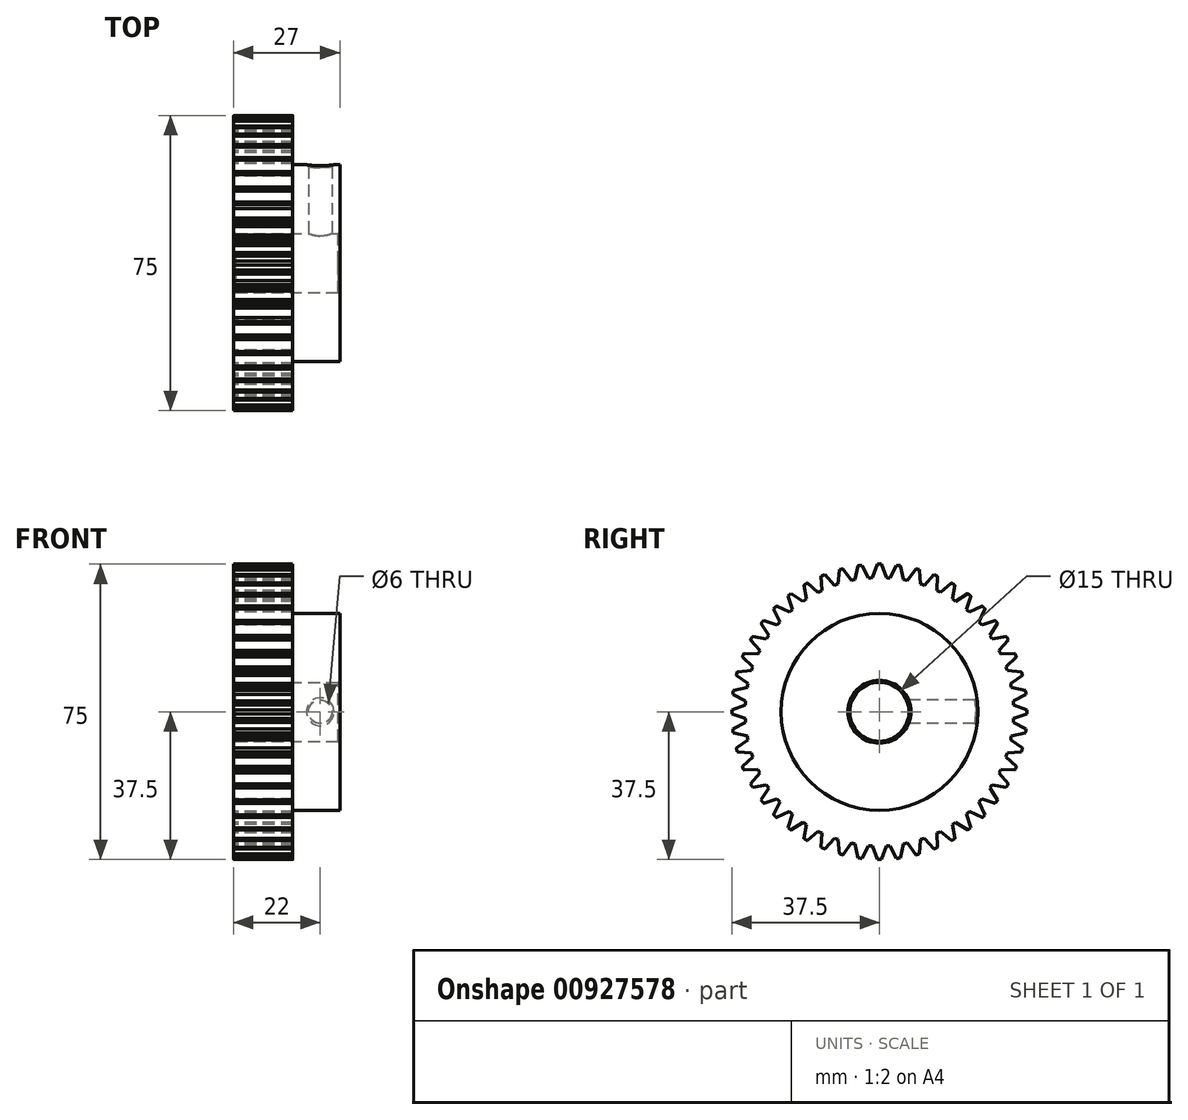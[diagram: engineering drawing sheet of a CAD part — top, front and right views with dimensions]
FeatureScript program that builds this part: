
annotation { "Feature Type Name" : "Feature", "Feature Type Description" : "" }
export const myFeature = defineFeature(function(context is Context, id is Id, definition is map)
    precondition{}
    {
        {
            var Q0;
            Q0=qCreatedBy(makeId("Right.planeOp"),FACE);
            var sketch = newSketch(context, id + "F0", { "sketchPlane" : qUnion([Q0])});
            skCircle(sketch, "E0", {"center": v(0, 0) * mm, "radius": 37.5 * mm});
            skSolve(sketch);
        }
        {
            var Q0;
            Q0 = qSketchRegion(id + "F0", true);
            extrude(context, id + "F1", {"entities" : qUnion([Q0]), "oppositeDirection" : true, "depth" : 27 * mm, "offsetDistance" : 25 * mm});
        }
        {
            var Q0;
            Q0=makeQuery(id+"F1.opExtrude","CAP_FACE",FACE,{"disambiguationData":[OSD([sQuery(id+"F0.wireOp",EDGE,"E0")])],"isStart":true});
            var sketch = newSketch(context, id + "F2", { "sketchPlane" : qUnion([Q0])});
            skCircle(sketch, "E1", {"center": v(0, 0) * mm, "radius": 7.5 * mm});
            skSolve(sketch);
        }
        {
            var Q0;
            Q0 = qSketchRegion(id + "F2", true);
            extrude(context, id + "F3", {"entities" : qUnion([Q0]), "operationType" : NewBodyOperationType.REMOVE, "endBound" : BoundingType.THROUGH_ALL, "oppositeDirection" : true, "depth" : 25 * mm, "offsetDistance" : 25 * mm});
        }
        {
            var Q0;
            Q0=makeQuery(id+"F3.boolean.opBoolean","COPY",FACE,{"derivedFrom":makeQuery(id+"F3.opExtrude","SWEPT_FACE",FACE,{"disambiguationData":[OSD([sQuery(id+"F2.wireOp",EDGE,"E1")])]})});
            chamfer(context, id + "F4", {"entities" : qUnion([Q0]), "width" : 0.5 * mm, "tangentPropagation" : true});
        }
        {
            var Q0;
            Q0=makeQuery(id+"F1.opExtrude","CAP_FACE",FACE,{"disambiguationData":[OSD([sQuery(id+"F0.wireOp",EDGE,"E0")])],"isStart":true});
            var sketch = newSketch(context, id + "F5", { "sketchPlane" : qUnion([Q0])});
            skCircle(sketch, "E2", {"center": v(0, 0) * mm, "radius": 25 * mm});
            skSolve(sketch);
        }
        {
            var Q0;
            Q0=makeQuery(id+"F5.imprint","IMPRINT",FACE,{"disambiguationData":[TD([[makeQuery(id+"F5.imprint","IMPRINT",EDGE,{"derivedFrom":sQuery(id+"F5.wireOp",EDGE,"E2")}),-1.0]])]});
            extrude(context, id + "F6", {"entities" : qUnion([Q0]), "operationType" : NewBodyOperationType.REMOVE, "oppositeDirection" : true, "depth" : 12 * mm, "offsetDistance" : 25 * mm});
        }
        {
            var Q0;
            Q0=makeQuery(id+"F1.opExtrude","CAP_FACE",FACE,{"disambiguationData":[OSD([sQuery(id+"F0.wireOp",EDGE,"E0")])],"isStart":false});
            var sketch = newSketch(context, id + "F7", { "sketchPlane" : qUnion([Q0])});
            skCircle(sketch, "E3", {"center": v(0, 0) * mm, "radius": 34.12 * mm, "construction": true});
            skLineSegment(sketch, "E4", {"start": v(0, 50.65) * mm, "end": v(0, 0) * mm, "construction": true});
            skLineSegment(sketch, "E5", {"start": v(0, 0) * mm, "end": v(6.76, 51.35) * mm, "construction": true});
            skLineSegment(sketch, "E6", {"start": v(0, 0) * mm, "end": v(3.18, 48.48) * mm, "construction": true});
            skLineSegment(sketch, "E7", {"start": v(0, 37.5) * mm, "end": v(0.5, 37.5) * mm});
            skLineSegment(sketch, "E8", {"start": v(4.9, 37.18) * mm, "end": v(4.4, 37.24) * mm});
            skLineSegment(sketch, "E9", {"start": v(2.23, 34.05) * mm, "end": v(2.73, 34.02) * mm});
            skLineSegment(sketch, "E10.MirrorCS", {"start": v(2.23, 34.05) * mm, "end": v(1.73, 34.08) * mm});
            skLineSegment(sketch, "E11", {"start": v(4.4, 37.24) * mm, "end": v(2.73, 34.02) * mm});
            skLineSegment(sketch, "E12", {"start": v(0.5, 37.5) * mm, "end": v(1.73, 34.08) * mm});
            skLineSegment(sketch, "E13.1.0", {"start": v(0, 0) * mm, "end": v(0, 51.8) * mm, "construction": true});
            skLineSegment(sketch, "E13.1.1", {"start": v(0, 37.5) * mm, "end": v(-0.5, 37.5) * mm});
            skLineSegment(sketch, "E13.1.2", {"start": v(-0.5, 37.5) * mm, "end": v(-1.73, 34.08) * mm});
            skLineSegment(sketch, "E13.1.3", {"start": v(-2.23, 34.05) * mm, "end": v(-1.73, 34.08) * mm});
            skLineSegment(sketch, "E13.1.4", {"start": v(-2.23, 34.05) * mm, "end": v(-2.73, 34.02) * mm});
            skLineSegment(sketch, "E13.1.5", {"start": v(-4.4, 37.24) * mm, "end": v(-2.73, 34.02) * mm});
            skLineSegment(sketch, "E13.1.6", {"start": v(-4.9, 37.18) * mm, "end": v(-4.4, 37.24) * mm});
            skLineSegment(sketch, "E13.2.0", {"start": v(0, 0) * mm, "end": v(-6.76, 51.35) * mm, "construction": true});
            skLineSegment(sketch, "E13.2.1", {"start": v(-4.9, 37.18) * mm, "end": v(-5.4, 37.11) * mm});
            skLineSegment(sketch, "E13.2.2", {"start": v(-5.4, 37.11) * mm, "end": v(-6.17, 33.56) * mm});
            skLineSegment(sketch, "E13.2.3", {"start": v(-6.66, 33.47) * mm, "end": v(-6.17, 33.56) * mm});
            skLineSegment(sketch, "E13.2.4", {"start": v(-6.66, 33.47) * mm, "end": v(-7.15, 33.37) * mm});
            skLineSegment(sketch, "E13.2.5", {"start": v(-9.22, 36.35) * mm, "end": v(-7.15, 33.37) * mm});
            skLineSegment(sketch, "E13.2.6", {"start": v(-9.7, 36.22) * mm, "end": v(-9.22, 36.35) * mm});
            skLineSegment(sketch, "E13.3.0", {"start": v(0, 0) * mm, "end": v(-13.4, 50.03) * mm, "construction": true});
            skLineSegment(sketch, "E13.3.1", {"start": v(-9.7, 36.22) * mm, "end": v(-10.19, 36.09) * mm});
            skLineSegment(sketch, "E13.3.2", {"start": v(-10.19, 36.09) * mm, "end": v(-10.5, 32.47) * mm});
            skLineSegment(sketch, "E13.3.3", {"start": v(-10.97, 32.31) * mm, "end": v(-10.5, 32.47) * mm});
            skLineSegment(sketch, "E13.3.4", {"start": v(-10.97, 32.31) * mm, "end": v(-11.44, 32.15) * mm});
            skLineSegment(sketch, "E13.3.5", {"start": v(-13.89, 34.83) * mm, "end": v(-11.44, 32.15) * mm});
            skLineSegment(sketch, "E13.3.6", {"start": v(-14.35, 34.65) * mm, "end": v(-13.89, 34.83) * mm});
            skLineSegment(sketch, "E13.4.0", {"start": v(0, 0) * mm, "end": v(-19.82, 47.85) * mm, "construction": true});
            skLineSegment(sketch, "E13.4.1", {"start": v(-14.35, 34.65) * mm, "end": v(-14.81, 34.45) * mm});
            skLineSegment(sketch, "E13.4.2", {"start": v(-14.81, 34.45) * mm, "end": v(-14.64, 30.82) * mm});
            skLineSegment(sketch, "E13.4.3", {"start": v(-15.1, 30.6) * mm, "end": v(-14.64, 30.82) * mm});
            skLineSegment(sketch, "E13.4.4", {"start": v(-15.1, 30.6) * mm, "end": v(-15.54, 30.38) * mm});
            skLineSegment(sketch, "E13.4.5", {"start": v(-18.32, 32.72) * mm, "end": v(-15.54, 30.38) * mm});
            skLineSegment(sketch, "E13.4.6", {"start": v(-18.75, 32.48) * mm, "end": v(-18.32, 32.72) * mm});
            skLineSegment(sketch, "E13.5.0", {"start": v(0, 0) * mm, "end": v(-25.9, 44.85) * mm, "construction": true});
            skLineSegment(sketch, "E13.5.1", {"start": v(-18.75, 32.48) * mm, "end": v(-19.18, 32.22) * mm});
            skLineSegment(sketch, "E13.5.2", {"start": v(-19.18, 32.22) * mm, "end": v(-18.54, 28.65) * mm});
            skLineSegment(sketch, "E13.5.3", {"start": v(-18.96, 28.37) * mm, "end": v(-18.54, 28.65) * mm});
            skLineSegment(sketch, "E13.5.4", {"start": v(-18.96, 28.37) * mm, "end": v(-19.37, 28.1) * mm});
            skLineSegment(sketch, "E13.5.5", {"start": v(-22.43, 30.05) * mm, "end": v(-19.37, 28.1) * mm});
            skLineSegment(sketch, "E13.5.6", {"start": v(-22.83, 29.75) * mm, "end": v(-22.43, 30.05) * mm});
            skLineSegment(sketch, "E13.6.0", {"start": v(0, 0) * mm, "end": v(-31.53, 41.09) * mm, "construction": true});
            skLineSegment(sketch, "E13.6.1", {"start": v(-22.83, 29.75) * mm, "end": v(-23.22, 29.44) * mm});
            skLineSegment(sketch, "E13.6.2", {"start": v(-23.22, 29.44) * mm, "end": v(-22.12, 25.98) * mm});
            skLineSegment(sketch, "E13.6.3", {"start": v(-22.5, 25.66) * mm, "end": v(-22.12, 25.98) * mm});
            skLineSegment(sketch, "E13.6.4", {"start": v(-22.5, 25.66) * mm, "end": v(-22.87, 25.32) * mm});
            skLineSegment(sketch, "E13.6.5", {"start": v(-26.16, 26.87) * mm, "end": v(-22.87, 25.32) * mm});
            skLineSegment(sketch, "E13.6.6", {"start": v(-26.52, 26.52) * mm, "end": v(-26.16, 26.87) * mm});
            skLineSegment(sketch, "E13.7.0", {"start": v(0, 0) * mm, "end": v(-36.62, 36.62) * mm, "construction": true});
            skLineSegment(sketch, "E13.7.1", {"start": v(-26.52, 26.52) * mm, "end": v(-26.87, 26.16) * mm});
            skLineSegment(sketch, "E13.7.2", {"start": v(-26.87, 26.16) * mm, "end": v(-25.32, 22.87) * mm});
            skLineSegment(sketch, "E13.7.3", {"start": v(-25.66, 22.5) * mm, "end": v(-25.32, 22.87) * mm});
            skLineSegment(sketch, "E13.7.4", {"start": v(-25.66, 22.5) * mm, "end": v(-25.98, 22.12) * mm});
            skLineSegment(sketch, "E13.7.5", {"start": v(-29.44, 23.22) * mm, "end": v(-25.98, 22.12) * mm});
            skLineSegment(sketch, "E13.7.6", {"start": v(-29.75, 22.83) * mm, "end": v(-29.44, 23.22) * mm});
            skLineSegment(sketch, "E13.8.0", {"start": v(0, 0) * mm, "end": v(-41.09, 31.53) * mm, "construction": true});
            skLineSegment(sketch, "E13.8.1", {"start": v(-29.75, 22.83) * mm, "end": v(-30.05, 22.43) * mm});
            skLineSegment(sketch, "E13.8.2", {"start": v(-30.05, 22.43) * mm, "end": v(-28.1, 19.37) * mm});
            skLineSegment(sketch, "E13.8.3", {"start": v(-28.37, 18.96) * mm, "end": v(-28.1, 19.37) * mm});
            skLineSegment(sketch, "E13.8.4", {"start": v(-28.37, 18.96) * mm, "end": v(-28.65, 18.54) * mm});
            skLineSegment(sketch, "E13.8.5", {"start": v(-32.22, 19.18) * mm, "end": v(-28.65, 18.54) * mm});
            skLineSegment(sketch, "E13.8.6", {"start": v(-32.48, 18.75) * mm, "end": v(-32.22, 19.18) * mm});
            skLineSegment(sketch, "E13.9.0", {"start": v(0, 0) * mm, "end": v(-44.85, 25.9) * mm, "construction": true});
            skLineSegment(sketch, "E13.9.1", {"start": v(-32.48, 18.75) * mm, "end": v(-32.72, 18.32) * mm});
            skLineSegment(sketch, "E13.9.2", {"start": v(-32.72, 18.32) * mm, "end": v(-30.38, 15.54) * mm});
            skLineSegment(sketch, "E13.9.3", {"start": v(-30.6, 15.1) * mm, "end": v(-30.38, 15.54) * mm});
            skLineSegment(sketch, "E13.9.4", {"start": v(-30.6, 15.1) * mm, "end": v(-30.82, 14.64) * mm});
            skLineSegment(sketch, "E13.9.5", {"start": v(-34.45, 14.81) * mm, "end": v(-30.82, 14.64) * mm});
            skLineSegment(sketch, "E13.9.6", {"start": v(-34.65, 14.35) * mm, "end": v(-34.45, 14.81) * mm});
            skLineSegment(sketch, "E13.10.0", {"start": v(0, 0) * mm, "end": v(-47.85, 19.82) * mm, "construction": true});
            skLineSegment(sketch, "E13.10.1", {"start": v(-34.65, 14.35) * mm, "end": v(-34.83, 13.89) * mm});
            skLineSegment(sketch, "E13.10.2", {"start": v(-34.83, 13.89) * mm, "end": v(-32.15, 11.44) * mm});
            skLineSegment(sketch, "E13.10.3", {"start": v(-32.31, 10.97) * mm, "end": v(-32.15, 11.44) * mm});
            skLineSegment(sketch, "E13.10.4", {"start": v(-32.31, 10.97) * mm, "end": v(-32.47, 10.5) * mm});
            skLineSegment(sketch, "E13.10.5", {"start": v(-36.09, 10.19) * mm, "end": v(-32.47, 10.5) * mm});
            skLineSegment(sketch, "E13.10.6", {"start": v(-36.22, 9.7) * mm, "end": v(-36.09, 10.19) * mm});
            skLineSegment(sketch, "E13.11.0", {"start": v(0, 0) * mm, "end": v(-50.03, 13.4) * mm, "construction": true});
            skLineSegment(sketch, "E13.11.1", {"start": v(-36.22, 9.7) * mm, "end": v(-36.35, 9.22) * mm});
            skLineSegment(sketch, "E13.11.2", {"start": v(-36.35, 9.22) * mm, "end": v(-33.37, 7.15) * mm});
            skLineSegment(sketch, "E13.11.3", {"start": v(-33.47, 6.66) * mm, "end": v(-33.37, 7.15) * mm});
            skLineSegment(sketch, "E13.11.4", {"start": v(-33.47, 6.66) * mm, "end": v(-33.56, 6.17) * mm});
            skLineSegment(sketch, "E13.11.5", {"start": v(-37.11, 5.4) * mm, "end": v(-33.56, 6.17) * mm});
            skLineSegment(sketch, "E13.11.6", {"start": v(-37.18, 4.9) * mm, "end": v(-37.11, 5.4) * mm});
            skLineSegment(sketch, "E13.12.0", {"start": v(0, 0) * mm, "end": v(-51.35, 6.76) * mm, "construction": true});
            skLineSegment(sketch, "E13.12.1", {"start": v(-37.18, 4.9) * mm, "end": v(-37.24, 4.4) * mm});
            skLineSegment(sketch, "E13.12.2", {"start": v(-37.24, 4.4) * mm, "end": v(-34.02, 2.73) * mm});
            skLineSegment(sketch, "E13.12.3", {"start": v(-34.05, 2.23) * mm, "end": v(-34.02, 2.73) * mm});
            skLineSegment(sketch, "E13.12.4", {"start": v(-34.05, 2.23) * mm, "end": v(-34.08, 1.73) * mm});
            skLineSegment(sketch, "E13.12.5", {"start": v(-37.5, 0.5) * mm, "end": v(-34.08, 1.73) * mm});
            skLineSegment(sketch, "E13.12.6", {"start": v(-37.5, 0) * mm, "end": v(-37.5, 0.5) * mm});
            skLineSegment(sketch, "E13.13.0", {"start": v(0, 0) * mm, "end": v(-51.8, 0) * mm, "construction": true});
            skLineSegment(sketch, "E13.13.1", {"start": v(-37.5, 0) * mm, "end": v(-37.5, -0.5) * mm});
            skLineSegment(sketch, "E13.13.2", {"start": v(-37.5, -0.5) * mm, "end": v(-34.08, -1.73) * mm});
            skLineSegment(sketch, "E13.13.3", {"start": v(-34.05, -2.23) * mm, "end": v(-34.08, -1.73) * mm});
            skLineSegment(sketch, "E13.13.4", {"start": v(-34.05, -2.23) * mm, "end": v(-34.02, -2.73) * mm});
            skLineSegment(sketch, "E13.13.5", {"start": v(-37.24, -4.4) * mm, "end": v(-34.02, -2.73) * mm});
            skLineSegment(sketch, "E13.13.6", {"start": v(-37.18, -4.9) * mm, "end": v(-37.24, -4.4) * mm});
            skLineSegment(sketch, "E13.14.0", {"start": v(0, 0) * mm, "end": v(-51.35, -6.76) * mm, "construction": true});
            skLineSegment(sketch, "E13.14.1", {"start": v(-37.18, -4.9) * mm, "end": v(-37.11, -5.4) * mm});
            skLineSegment(sketch, "E13.14.2", {"start": v(-37.11, -5.4) * mm, "end": v(-33.56, -6.17) * mm});
            skLineSegment(sketch, "E13.14.3", {"start": v(-33.47, -6.66) * mm, "end": v(-33.56, -6.17) * mm});
            skLineSegment(sketch, "E13.14.4", {"start": v(-33.47, -6.66) * mm, "end": v(-33.37, -7.15) * mm});
            skLineSegment(sketch, "E13.14.5", {"start": v(-36.35, -9.22) * mm, "end": v(-33.37, -7.15) * mm});
            skLineSegment(sketch, "E13.14.6", {"start": v(-36.22, -9.7) * mm, "end": v(-36.35, -9.22) * mm});
            skLineSegment(sketch, "E13.15.0", {"start": v(0, 0) * mm, "end": v(-50.03, -13.4) * mm, "construction": true});
            skLineSegment(sketch, "E13.15.1", {"start": v(-36.22, -9.7) * mm, "end": v(-36.09, -10.19) * mm});
            skLineSegment(sketch, "E13.15.2", {"start": v(-36.09, -10.19) * mm, "end": v(-32.47, -10.5) * mm});
            skLineSegment(sketch, "E13.15.3", {"start": v(-32.31, -10.97) * mm, "end": v(-32.47, -10.5) * mm});
            skLineSegment(sketch, "E13.15.4", {"start": v(-32.31, -10.97) * mm, "end": v(-32.15, -11.44) * mm});
            skLineSegment(sketch, "E13.15.5", {"start": v(-34.83, -13.89) * mm, "end": v(-32.15, -11.44) * mm});
            skLineSegment(sketch, "E13.15.6", {"start": v(-34.65, -14.35) * mm, "end": v(-34.83, -13.89) * mm});
            skLineSegment(sketch, "E13.16.0", {"start": v(0, 0) * mm, "end": v(-47.85, -19.82) * mm, "construction": true});
            skLineSegment(sketch, "E13.16.1", {"start": v(-34.65, -14.35) * mm, "end": v(-34.45, -14.81) * mm});
            skLineSegment(sketch, "E13.16.2", {"start": v(-34.45, -14.81) * mm, "end": v(-30.82, -14.64) * mm});
            skLineSegment(sketch, "E13.16.3", {"start": v(-30.6, -15.1) * mm, "end": v(-30.82, -14.64) * mm});
            skLineSegment(sketch, "E13.16.4", {"start": v(-30.6, -15.1) * mm, "end": v(-30.38, -15.54) * mm});
            skLineSegment(sketch, "E13.16.5", {"start": v(-32.72, -18.32) * mm, "end": v(-30.38, -15.54) * mm});
            skLineSegment(sketch, "E13.16.6", {"start": v(-32.48, -18.75) * mm, "end": v(-32.72, -18.32) * mm});
            skLineSegment(sketch, "E13.17.0", {"start": v(0, 0) * mm, "end": v(-44.85, -25.9) * mm, "construction": true});
            skLineSegment(sketch, "E13.17.1", {"start": v(-32.48, -18.75) * mm, "end": v(-32.22, -19.18) * mm});
            skLineSegment(sketch, "E13.17.2", {"start": v(-32.22, -19.18) * mm, "end": v(-28.65, -18.54) * mm});
            skLineSegment(sketch, "E13.17.3", {"start": v(-28.37, -18.96) * mm, "end": v(-28.65, -18.54) * mm});
            skLineSegment(sketch, "E13.17.4", {"start": v(-28.37, -18.96) * mm, "end": v(-28.1, -19.37) * mm});
            skLineSegment(sketch, "E13.17.5", {"start": v(-30.05, -22.43) * mm, "end": v(-28.1, -19.37) * mm});
            skLineSegment(sketch, "E13.17.6", {"start": v(-29.75, -22.83) * mm, "end": v(-30.05, -22.43) * mm});
            skLineSegment(sketch, "E13.18.0", {"start": v(0, 0) * mm, "end": v(-41.09, -31.53) * mm, "construction": true});
            skLineSegment(sketch, "E13.18.1", {"start": v(-29.75, -22.83) * mm, "end": v(-29.44, -23.22) * mm});
            skLineSegment(sketch, "E13.18.2", {"start": v(-29.44, -23.22) * mm, "end": v(-25.98, -22.12) * mm});
            skLineSegment(sketch, "E13.18.3", {"start": v(-25.66, -22.5) * mm, "end": v(-25.98, -22.12) * mm});
            skLineSegment(sketch, "E13.18.4", {"start": v(-25.66, -22.5) * mm, "end": v(-25.32, -22.87) * mm});
            skLineSegment(sketch, "E13.18.5", {"start": v(-26.87, -26.16) * mm, "end": v(-25.32, -22.87) * mm});
            skLineSegment(sketch, "E13.18.6", {"start": v(-26.52, -26.52) * mm, "end": v(-26.87, -26.16) * mm});
            skLineSegment(sketch, "E13.19.0", {"start": v(0, 0) * mm, "end": v(-36.62, -36.62) * mm, "construction": true});
            skLineSegment(sketch, "E13.19.1", {"start": v(-26.52, -26.52) * mm, "end": v(-26.16, -26.87) * mm});
            skLineSegment(sketch, "E13.19.2", {"start": v(-26.16, -26.87) * mm, "end": v(-22.87, -25.32) * mm});
            skLineSegment(sketch, "E13.19.3", {"start": v(-22.5, -25.66) * mm, "end": v(-22.87, -25.32) * mm});
            skLineSegment(sketch, "E13.19.4", {"start": v(-22.5, -25.66) * mm, "end": v(-22.12, -25.98) * mm});
            skLineSegment(sketch, "E13.19.5", {"start": v(-23.22, -29.44) * mm, "end": v(-22.12, -25.98) * mm});
            skLineSegment(sketch, "E13.19.6", {"start": v(-22.83, -29.75) * mm, "end": v(-23.22, -29.44) * mm});
            skLineSegment(sketch, "E13.20.0", {"start": v(0, 0) * mm, "end": v(-31.53, -41.09) * mm, "construction": true});
            skLineSegment(sketch, "E13.20.1", {"start": v(-22.83, -29.75) * mm, "end": v(-22.43, -30.05) * mm});
            skLineSegment(sketch, "E13.20.2", {"start": v(-22.43, -30.05) * mm, "end": v(-19.37, -28.1) * mm});
            skLineSegment(sketch, "E13.20.3", {"start": v(-18.96, -28.37) * mm, "end": v(-19.37, -28.1) * mm});
            skLineSegment(sketch, "E13.20.4", {"start": v(-18.96, -28.37) * mm, "end": v(-18.54, -28.65) * mm});
            skLineSegment(sketch, "E13.20.5", {"start": v(-19.18, -32.22) * mm, "end": v(-18.54, -28.65) * mm});
            skLineSegment(sketch, "E13.20.6", {"start": v(-18.75, -32.48) * mm, "end": v(-19.18, -32.22) * mm});
            skLineSegment(sketch, "E13.21.0", {"start": v(0, 0) * mm, "end": v(-25.9, -44.85) * mm, "construction": true});
            skLineSegment(sketch, "E13.21.1", {"start": v(-18.75, -32.48) * mm, "end": v(-18.32, -32.72) * mm});
            skLineSegment(sketch, "E13.21.2", {"start": v(-18.32, -32.72) * mm, "end": v(-15.54, -30.38) * mm});
            skLineSegment(sketch, "E13.21.3", {"start": v(-15.1, -30.6) * mm, "end": v(-15.54, -30.38) * mm});
            skLineSegment(sketch, "E13.21.4", {"start": v(-15.1, -30.6) * mm, "end": v(-14.64, -30.82) * mm});
            skLineSegment(sketch, "E13.21.5", {"start": v(-14.81, -34.45) * mm, "end": v(-14.64, -30.82) * mm});
            skLineSegment(sketch, "E13.21.6", {"start": v(-14.35, -34.65) * mm, "end": v(-14.81, -34.45) * mm});
            skLineSegment(sketch, "E13.22.0", {"start": v(0, 0) * mm, "end": v(-19.82, -47.85) * mm, "construction": true});
            skLineSegment(sketch, "E13.22.1", {"start": v(-14.35, -34.65) * mm, "end": v(-13.89, -34.83) * mm});
            skLineSegment(sketch, "E13.22.2", {"start": v(-13.89, -34.83) * mm, "end": v(-11.44, -32.15) * mm});
            skLineSegment(sketch, "E13.22.3", {"start": v(-10.97, -32.31) * mm, "end": v(-11.44, -32.15) * mm});
            skLineSegment(sketch, "E13.22.4", {"start": v(-10.97, -32.31) * mm, "end": v(-10.5, -32.47) * mm});
            skLineSegment(sketch, "E13.22.5", {"start": v(-10.19, -36.09) * mm, "end": v(-10.5, -32.47) * mm});
            skLineSegment(sketch, "E13.22.6", {"start": v(-9.7, -36.22) * mm, "end": v(-10.19, -36.09) * mm});
            skLineSegment(sketch, "E13.23.0", {"start": v(0, 0) * mm, "end": v(-13.4, -50.03) * mm, "construction": true});
            skLineSegment(sketch, "E13.23.1", {"start": v(-9.7, -36.22) * mm, "end": v(-9.22, -36.35) * mm});
            skLineSegment(sketch, "E13.23.2", {"start": v(-9.22, -36.35) * mm, "end": v(-7.15, -33.37) * mm});
            skLineSegment(sketch, "E13.23.3", {"start": v(-6.66, -33.47) * mm, "end": v(-7.15, -33.37) * mm});
            skLineSegment(sketch, "E13.23.4", {"start": v(-6.66, -33.47) * mm, "end": v(-6.17, -33.56) * mm});
            skLineSegment(sketch, "E13.23.5", {"start": v(-5.4, -37.11) * mm, "end": v(-6.17, -33.56) * mm});
            skLineSegment(sketch, "E13.23.6", {"start": v(-4.9, -37.18) * mm, "end": v(-5.4, -37.11) * mm});
            skLineSegment(sketch, "E13.24.0", {"start": v(0, 0) * mm, "end": v(-6.76, -51.35) * mm, "construction": true});
            skLineSegment(sketch, "E13.24.1", {"start": v(-4.9, -37.18) * mm, "end": v(-4.4, -37.24) * mm});
            skLineSegment(sketch, "E13.24.2", {"start": v(-4.4, -37.24) * mm, "end": v(-2.73, -34.02) * mm});
            skLineSegment(sketch, "E13.24.3", {"start": v(-2.23, -34.05) * mm, "end": v(-2.73, -34.02) * mm});
            skLineSegment(sketch, "E13.24.4", {"start": v(-2.23, -34.05) * mm, "end": v(-1.73, -34.08) * mm});
            skLineSegment(sketch, "E13.24.5", {"start": v(-0.5, -37.5) * mm, "end": v(-1.73, -34.08) * mm});
            skLineSegment(sketch, "E13.24.6", {"start": v(0, -37.5) * mm, "end": v(-0.5, -37.5) * mm});
            skLineSegment(sketch, "E13.25.0", {"start": v(0, 0) * mm, "end": v(0, -51.8) * mm, "construction": true});
            skLineSegment(sketch, "E13.25.1", {"start": v(0, -37.5) * mm, "end": v(0.5, -37.5) * mm});
            skLineSegment(sketch, "E13.25.2", {"start": v(0.5, -37.5) * mm, "end": v(1.73, -34.08) * mm});
            skLineSegment(sketch, "E13.25.3", {"start": v(2.23, -34.05) * mm, "end": v(1.73, -34.08) * mm});
            skLineSegment(sketch, "E13.25.4", {"start": v(2.23, -34.05) * mm, "end": v(2.73, -34.02) * mm});
            skLineSegment(sketch, "E13.25.5", {"start": v(4.4, -37.24) * mm, "end": v(2.73, -34.02) * mm});
            skLineSegment(sketch, "E13.25.6", {"start": v(4.9, -37.18) * mm, "end": v(4.4, -37.24) * mm});
            skLineSegment(sketch, "E13.26.0", {"start": v(0, 0) * mm, "end": v(6.76, -51.35) * mm, "construction": true});
            skLineSegment(sketch, "E13.26.1", {"start": v(4.9, -37.18) * mm, "end": v(5.4, -37.11) * mm});
            skLineSegment(sketch, "E13.26.2", {"start": v(5.4, -37.11) * mm, "end": v(6.17, -33.56) * mm});
            skLineSegment(sketch, "E13.26.3", {"start": v(6.66, -33.47) * mm, "end": v(6.17, -33.56) * mm});
            skLineSegment(sketch, "E13.26.4", {"start": v(6.66, -33.47) * mm, "end": v(7.15, -33.37) * mm});
            skLineSegment(sketch, "E13.26.5", {"start": v(9.22, -36.35) * mm, "end": v(7.15, -33.37) * mm});
            skLineSegment(sketch, "E13.26.6", {"start": v(9.7, -36.22) * mm, "end": v(9.22, -36.35) * mm});
            skLineSegment(sketch, "E13.27.0", {"start": v(0, 0) * mm, "end": v(13.4, -50.03) * mm, "construction": true});
            skLineSegment(sketch, "E13.27.1", {"start": v(9.7, -36.22) * mm, "end": v(10.19, -36.09) * mm});
            skLineSegment(sketch, "E13.27.2", {"start": v(10.19, -36.09) * mm, "end": v(10.5, -32.47) * mm});
            skLineSegment(sketch, "E13.27.3", {"start": v(10.97, -32.31) * mm, "end": v(10.5, -32.47) * mm});
            skLineSegment(sketch, "E13.27.4", {"start": v(10.97, -32.31) * mm, "end": v(11.44, -32.15) * mm});
            skLineSegment(sketch, "E13.27.5", {"start": v(13.89, -34.83) * mm, "end": v(11.44, -32.15) * mm});
            skLineSegment(sketch, "E13.27.6", {"start": v(14.35, -34.65) * mm, "end": v(13.89, -34.83) * mm});
            skLineSegment(sketch, "E13.28.0", {"start": v(0, 0) * mm, "end": v(19.82, -47.85) * mm, "construction": true});
            skLineSegment(sketch, "E13.28.1", {"start": v(14.35, -34.65) * mm, "end": v(14.81, -34.45) * mm});
            skLineSegment(sketch, "E13.28.2", {"start": v(14.81, -34.45) * mm, "end": v(14.64, -30.82) * mm});
            skLineSegment(sketch, "E13.28.3", {"start": v(15.1, -30.6) * mm, "end": v(14.64, -30.82) * mm});
            skLineSegment(sketch, "E13.28.4", {"start": v(15.1, -30.6) * mm, "end": v(15.54, -30.38) * mm});
            skLineSegment(sketch, "E13.28.5", {"start": v(18.32, -32.72) * mm, "end": v(15.54, -30.38) * mm});
            skLineSegment(sketch, "E13.28.6", {"start": v(18.75, -32.48) * mm, "end": v(18.32, -32.72) * mm});
            skLineSegment(sketch, "E13.29.0", {"start": v(0, 0) * mm, "end": v(25.9, -44.85) * mm, "construction": true});
            skLineSegment(sketch, "E13.29.1", {"start": v(18.75, -32.48) * mm, "end": v(19.18, -32.22) * mm});
            skLineSegment(sketch, "E13.29.2", {"start": v(19.18, -32.22) * mm, "end": v(18.54, -28.65) * mm});
            skLineSegment(sketch, "E13.29.3", {"start": v(18.96, -28.37) * mm, "end": v(18.54, -28.65) * mm});
            skLineSegment(sketch, "E13.29.4", {"start": v(18.96, -28.37) * mm, "end": v(19.37, -28.1) * mm});
            skLineSegment(sketch, "E13.29.5", {"start": v(22.43, -30.05) * mm, "end": v(19.37, -28.1) * mm});
            skLineSegment(sketch, "E13.29.6", {"start": v(22.83, -29.75) * mm, "end": v(22.43, -30.05) * mm});
            skLineSegment(sketch, "E13.30.0", {"start": v(0, 0) * mm, "end": v(31.53, -41.09) * mm, "construction": true});
            skLineSegment(sketch, "E13.30.1", {"start": v(22.83, -29.75) * mm, "end": v(23.22, -29.44) * mm});
            skLineSegment(sketch, "E13.30.2", {"start": v(23.22, -29.44) * mm, "end": v(22.12, -25.98) * mm});
            skLineSegment(sketch, "E13.30.3", {"start": v(22.5, -25.66) * mm, "end": v(22.12, -25.98) * mm});
            skLineSegment(sketch, "E13.30.4", {"start": v(22.5, -25.66) * mm, "end": v(22.87, -25.32) * mm});
            skLineSegment(sketch, "E13.30.5", {"start": v(26.16, -26.87) * mm, "end": v(22.87, -25.32) * mm});
            skLineSegment(sketch, "E13.30.6", {"start": v(26.52, -26.52) * mm, "end": v(26.16, -26.87) * mm});
            skLineSegment(sketch, "E13.31.0", {"start": v(0, 0) * mm, "end": v(36.62, -36.62) * mm, "construction": true});
            skLineSegment(sketch, "E13.31.1", {"start": v(26.52, -26.52) * mm, "end": v(26.87, -26.16) * mm});
            skLineSegment(sketch, "E13.31.2", {"start": v(26.87, -26.16) * mm, "end": v(25.32, -22.87) * mm});
            skLineSegment(sketch, "E13.31.3", {"start": v(25.66, -22.5) * mm, "end": v(25.32, -22.87) * mm});
            skLineSegment(sketch, "E13.31.4", {"start": v(25.66, -22.5) * mm, "end": v(25.98, -22.12) * mm});
            skLineSegment(sketch, "E13.31.5", {"start": v(29.44, -23.22) * mm, "end": v(25.98, -22.12) * mm});
            skLineSegment(sketch, "E13.31.6", {"start": v(29.75, -22.83) * mm, "end": v(29.44, -23.22) * mm});
            skLineSegment(sketch, "E13.32.0", {"start": v(0, 0) * mm, "end": v(41.09, -31.53) * mm, "construction": true});
            skLineSegment(sketch, "E13.32.1", {"start": v(29.75, -22.83) * mm, "end": v(30.05, -22.43) * mm});
            skLineSegment(sketch, "E13.32.2", {"start": v(30.05, -22.43) * mm, "end": v(28.1, -19.37) * mm});
            skLineSegment(sketch, "E13.32.3", {"start": v(28.37, -18.96) * mm, "end": v(28.1, -19.37) * mm});
            skLineSegment(sketch, "E13.32.4", {"start": v(28.37, -18.96) * mm, "end": v(28.65, -18.54) * mm});
            skLineSegment(sketch, "E13.32.5", {"start": v(32.22, -19.18) * mm, "end": v(28.65, -18.54) * mm});
            skLineSegment(sketch, "E13.32.6", {"start": v(32.48, -18.75) * mm, "end": v(32.22, -19.18) * mm});
            skLineSegment(sketch, "E13.33.0", {"start": v(0, 0) * mm, "end": v(44.85, -25.9) * mm, "construction": true});
            skLineSegment(sketch, "E13.33.1", {"start": v(32.48, -18.75) * mm, "end": v(32.72, -18.32) * mm});
            skLineSegment(sketch, "E13.33.2", {"start": v(32.72, -18.32) * mm, "end": v(30.38, -15.54) * mm});
            skLineSegment(sketch, "E13.33.3", {"start": v(30.6, -15.1) * mm, "end": v(30.38, -15.54) * mm});
            skLineSegment(sketch, "E13.33.4", {"start": v(30.6, -15.1) * mm, "end": v(30.82, -14.64) * mm});
            skLineSegment(sketch, "E13.33.5", {"start": v(34.45, -14.81) * mm, "end": v(30.82, -14.64) * mm});
            skLineSegment(sketch, "E13.33.6", {"start": v(34.65, -14.35) * mm, "end": v(34.45, -14.81) * mm});
            skLineSegment(sketch, "E13.34.0", {"start": v(0, 0) * mm, "end": v(47.85, -19.82) * mm, "construction": true});
            skLineSegment(sketch, "E13.34.1", {"start": v(34.65, -14.35) * mm, "end": v(34.83, -13.89) * mm});
            skLineSegment(sketch, "E13.34.2", {"start": v(34.83, -13.89) * mm, "end": v(32.15, -11.44) * mm});
            skLineSegment(sketch, "E13.34.3", {"start": v(32.31, -10.97) * mm, "end": v(32.15, -11.44) * mm});
            skLineSegment(sketch, "E13.34.4", {"start": v(32.31, -10.97) * mm, "end": v(32.47, -10.5) * mm});
            skLineSegment(sketch, "E13.34.5", {"start": v(36.09, -10.19) * mm, "end": v(32.47, -10.5) * mm});
            skLineSegment(sketch, "E13.34.6", {"start": v(36.22, -9.7) * mm, "end": v(36.09, -10.19) * mm});
            skLineSegment(sketch, "E13.35.0", {"start": v(0, 0) * mm, "end": v(50.03, -13.4) * mm, "construction": true});
            skLineSegment(sketch, "E13.35.1", {"start": v(36.22, -9.7) * mm, "end": v(36.35, -9.22) * mm});
            skLineSegment(sketch, "E13.35.2", {"start": v(36.35, -9.22) * mm, "end": v(33.37, -7.15) * mm});
            skLineSegment(sketch, "E13.35.3", {"start": v(33.47, -6.66) * mm, "end": v(33.37, -7.15) * mm});
            skLineSegment(sketch, "E13.35.4", {"start": v(33.47, -6.66) * mm, "end": v(33.56, -6.17) * mm});
            skLineSegment(sketch, "E13.35.5", {"start": v(37.11, -5.4) * mm, "end": v(33.56, -6.17) * mm});
            skLineSegment(sketch, "E13.35.6", {"start": v(37.18, -4.9) * mm, "end": v(37.11, -5.4) * mm});
            skLineSegment(sketch, "E13.36.0", {"start": v(0, 0) * mm, "end": v(51.35, -6.76) * mm, "construction": true});
            skLineSegment(sketch, "E13.36.1", {"start": v(37.18, -4.9) * mm, "end": v(37.24, -4.4) * mm});
            skLineSegment(sketch, "E13.36.2", {"start": v(37.24, -4.4) * mm, "end": v(34.02, -2.73) * mm});
            skLineSegment(sketch, "E13.36.3", {"start": v(34.05, -2.23) * mm, "end": v(34.02, -2.73) * mm});
            skLineSegment(sketch, "E13.36.4", {"start": v(34.05, -2.23) * mm, "end": v(34.08, -1.73) * mm});
            skLineSegment(sketch, "E13.36.5", {"start": v(37.5, -0.5) * mm, "end": v(34.08, -1.73) * mm});
            skLineSegment(sketch, "E13.36.6", {"start": v(37.5, 0) * mm, "end": v(37.5, -0.5) * mm});
            skLineSegment(sketch, "E13.37.0", {"start": v(0, 0) * mm, "end": v(51.8, 0) * mm, "construction": true});
            skLineSegment(sketch, "E13.37.1", {"start": v(37.5, 0) * mm, "end": v(37.5, 0.5) * mm});
            skLineSegment(sketch, "E13.37.2", {"start": v(37.5, 0.5) * mm, "end": v(34.08, 1.73) * mm});
            skLineSegment(sketch, "E13.37.3", {"start": v(34.05, 2.23) * mm, "end": v(34.08, 1.73) * mm});
            skLineSegment(sketch, "E13.37.4", {"start": v(34.05, 2.23) * mm, "end": v(34.02, 2.73) * mm});
            skLineSegment(sketch, "E13.37.5", {"start": v(37.24, 4.4) * mm, "end": v(34.02, 2.73) * mm});
            skLineSegment(sketch, "E13.37.6", {"start": v(37.18, 4.9) * mm, "end": v(37.24, 4.4) * mm});
            skLineSegment(sketch, "E13.38.0", {"start": v(0, 0) * mm, "end": v(51.35, 6.76) * mm, "construction": true});
            skLineSegment(sketch, "E13.38.1", {"start": v(37.18, 4.9) * mm, "end": v(37.11, 5.4) * mm});
            skLineSegment(sketch, "E13.38.2", {"start": v(37.11, 5.4) * mm, "end": v(33.56, 6.17) * mm});
            skLineSegment(sketch, "E13.38.3", {"start": v(33.47, 6.66) * mm, "end": v(33.56, 6.17) * mm});
            skLineSegment(sketch, "E13.38.4", {"start": v(33.47, 6.66) * mm, "end": v(33.37, 7.15) * mm});
            skLineSegment(sketch, "E13.38.5", {"start": v(36.35, 9.22) * mm, "end": v(33.37, 7.15) * mm});
            skLineSegment(sketch, "E13.38.6", {"start": v(36.22, 9.7) * mm, "end": v(36.35, 9.22) * mm});
            skLineSegment(sketch, "E13.39.0", {"start": v(0, 0) * mm, "end": v(50.03, 13.4) * mm, "construction": true});
            skLineSegment(sketch, "E13.39.1", {"start": v(36.22, 9.7) * mm, "end": v(36.09, 10.19) * mm});
            skLineSegment(sketch, "E13.39.2", {"start": v(36.09, 10.19) * mm, "end": v(32.47, 10.5) * mm});
            skLineSegment(sketch, "E13.39.3", {"start": v(32.31, 10.97) * mm, "end": v(32.47, 10.5) * mm});
            skLineSegment(sketch, "E13.39.4", {"start": v(32.31, 10.97) * mm, "end": v(32.15, 11.44) * mm});
            skLineSegment(sketch, "E13.39.5", {"start": v(34.83, 13.89) * mm, "end": v(32.15, 11.44) * mm});
            skLineSegment(sketch, "E13.39.6", {"start": v(34.65, 14.35) * mm, "end": v(34.83, 13.89) * mm});
            skLineSegment(sketch, "E13.40.0", {"start": v(0, 0) * mm, "end": v(47.85, 19.82) * mm, "construction": true});
            skLineSegment(sketch, "E13.40.1", {"start": v(34.65, 14.35) * mm, "end": v(34.45, 14.81) * mm});
            skLineSegment(sketch, "E13.40.2", {"start": v(34.45, 14.81) * mm, "end": v(30.82, 14.64) * mm});
            skLineSegment(sketch, "E13.40.3", {"start": v(30.6, 15.1) * mm, "end": v(30.82, 14.64) * mm});
            skLineSegment(sketch, "E13.40.4", {"start": v(30.6, 15.1) * mm, "end": v(30.38, 15.54) * mm});
            skLineSegment(sketch, "E13.40.5", {"start": v(32.72, 18.32) * mm, "end": v(30.38, 15.54) * mm});
            skLineSegment(sketch, "E13.40.6", {"start": v(32.48, 18.75) * mm, "end": v(32.72, 18.32) * mm});
            skLineSegment(sketch, "E13.41.0", {"start": v(0, 0) * mm, "end": v(44.85, 25.9) * mm, "construction": true});
            skLineSegment(sketch, "E13.41.1", {"start": v(32.48, 18.75) * mm, "end": v(32.22, 19.18) * mm});
            skLineSegment(sketch, "E13.41.2", {"start": v(32.22, 19.18) * mm, "end": v(28.65, 18.54) * mm});
            skLineSegment(sketch, "E13.41.3", {"start": v(28.37, 18.96) * mm, "end": v(28.65, 18.54) * mm});
            skLineSegment(sketch, "E13.41.4", {"start": v(28.37, 18.96) * mm, "end": v(28.1, 19.37) * mm});
            skLineSegment(sketch, "E13.41.5", {"start": v(30.05, 22.43) * mm, "end": v(28.1, 19.37) * mm});
            skLineSegment(sketch, "E13.41.6", {"start": v(29.75, 22.83) * mm, "end": v(30.05, 22.43) * mm});
            skLineSegment(sketch, "E13.42.0", {"start": v(0, 0) * mm, "end": v(41.09, 31.53) * mm, "construction": true});
            skLineSegment(sketch, "E13.42.1", {"start": v(29.75, 22.83) * mm, "end": v(29.44, 23.22) * mm});
            skLineSegment(sketch, "E13.42.2", {"start": v(29.44, 23.22) * mm, "end": v(25.98, 22.12) * mm});
            skLineSegment(sketch, "E13.42.3", {"start": v(25.66, 22.5) * mm, "end": v(25.98, 22.12) * mm});
            skLineSegment(sketch, "E13.42.4", {"start": v(25.66, 22.5) * mm, "end": v(25.32, 22.87) * mm});
            skLineSegment(sketch, "E13.42.5", {"start": v(26.87, 26.16) * mm, "end": v(25.32, 22.87) * mm});
            skLineSegment(sketch, "E13.42.6", {"start": v(26.52, 26.52) * mm, "end": v(26.87, 26.16) * mm});
            skLineSegment(sketch, "E13.43.0", {"start": v(0, 0) * mm, "end": v(36.62, 36.62) * mm, "construction": true});
            skLineSegment(sketch, "E13.43.1", {"start": v(26.52, 26.52) * mm, "end": v(26.16, 26.87) * mm});
            skLineSegment(sketch, "E13.43.2", {"start": v(26.16, 26.87) * mm, "end": v(22.87, 25.32) * mm});
            skLineSegment(sketch, "E13.43.3", {"start": v(22.5, 25.66) * mm, "end": v(22.87, 25.32) * mm});
            skLineSegment(sketch, "E13.43.4", {"start": v(22.5, 25.66) * mm, "end": v(22.12, 25.98) * mm});
            skLineSegment(sketch, "E13.43.5", {"start": v(23.22, 29.44) * mm, "end": v(22.12, 25.98) * mm});
            skLineSegment(sketch, "E13.43.6", {"start": v(22.83, 29.75) * mm, "end": v(23.22, 29.44) * mm});
            skLineSegment(sketch, "E13.44.0", {"start": v(0, 0) * mm, "end": v(31.53, 41.09) * mm, "construction": true});
            skLineSegment(sketch, "E13.44.1", {"start": v(22.83, 29.75) * mm, "end": v(22.43, 30.05) * mm});
            skLineSegment(sketch, "E13.44.2", {"start": v(22.43, 30.05) * mm, "end": v(19.37, 28.1) * mm});
            skLineSegment(sketch, "E13.44.3", {"start": v(18.96, 28.37) * mm, "end": v(19.37, 28.1) * mm});
            skLineSegment(sketch, "E13.44.4", {"start": v(18.96, 28.37) * mm, "end": v(18.54, 28.65) * mm});
            skLineSegment(sketch, "E13.44.5", {"start": v(19.18, 32.22) * mm, "end": v(18.54, 28.65) * mm});
            skLineSegment(sketch, "E13.44.6", {"start": v(18.75, 32.48) * mm, "end": v(19.18, 32.22) * mm});
            skLineSegment(sketch, "E13.45.0", {"start": v(0, 0) * mm, "end": v(25.9, 44.85) * mm, "construction": true});
            skLineSegment(sketch, "E13.45.1", {"start": v(18.75, 32.48) * mm, "end": v(18.32, 32.72) * mm});
            skLineSegment(sketch, "E13.45.2", {"start": v(18.32, 32.72) * mm, "end": v(15.54, 30.38) * mm});
            skLineSegment(sketch, "E13.45.3", {"start": v(15.1, 30.6) * mm, "end": v(15.54, 30.38) * mm});
            skLineSegment(sketch, "E13.45.4", {"start": v(15.1, 30.6) * mm, "end": v(14.64, 30.82) * mm});
            skLineSegment(sketch, "E13.45.5", {"start": v(14.81, 34.45) * mm, "end": v(14.64, 30.82) * mm});
            skLineSegment(sketch, "E13.45.6", {"start": v(14.35, 34.65) * mm, "end": v(14.81, 34.45) * mm});
            skLineSegment(sketch, "E13.46.0", {"start": v(0, 0) * mm, "end": v(19.82, 47.85) * mm, "construction": true});
            skLineSegment(sketch, "E13.46.1", {"start": v(14.35, 34.65) * mm, "end": v(13.89, 34.83) * mm});
            skLineSegment(sketch, "E13.46.2", {"start": v(13.89, 34.83) * mm, "end": v(11.44, 32.15) * mm});
            skLineSegment(sketch, "E13.46.3", {"start": v(10.97, 32.31) * mm, "end": v(11.44, 32.15) * mm});
            skLineSegment(sketch, "E13.46.4", {"start": v(10.97, 32.31) * mm, "end": v(10.5, 32.47) * mm});
            skLineSegment(sketch, "E13.46.5", {"start": v(10.19, 36.09) * mm, "end": v(10.5, 32.47) * mm});
            skLineSegment(sketch, "E13.46.6", {"start": v(9.7, 36.22) * mm, "end": v(10.19, 36.09) * mm});
            skLineSegment(sketch, "E13.47.0", {"start": v(0, 0) * mm, "end": v(13.4, 50.03) * mm, "construction": true});
            skLineSegment(sketch, "E13.47.1", {"start": v(9.7, 36.22) * mm, "end": v(9.22, 36.35) * mm});
            skLineSegment(sketch, "E13.47.2", {"start": v(9.22, 36.35) * mm, "end": v(7.15, 33.37) * mm});
            skLineSegment(sketch, "E13.47.3", {"start": v(6.66, 33.47) * mm, "end": v(7.15, 33.37) * mm});
            skLineSegment(sketch, "E13.47.4", {"start": v(6.66, 33.47) * mm, "end": v(6.17, 33.56) * mm});
            skLineSegment(sketch, "E13.47.5", {"start": v(5.4, 37.11) * mm, "end": v(6.17, 33.56) * mm});
            skLineSegment(sketch, "E13.47.6", {"start": v(4.9, 37.18) * mm, "end": v(5.4, 37.11) * mm});
            skSolve(sketch);
        }
        {
            var Q0;
            {var subQ1=sQuery(id+"F7.wireOp",EDGE,"E13.6.2");Q0=makeQuery(id+"F7.imprint","IMPRINT",FACE,{"disambiguationData":[TD([[makeQuery(id+"F7.imprint","IMPRINT",EDGE,{"derivedFrom":subQ1}),-1.0]])]});}
            var Q1;
            {var subQ1=sQuery(id+"F7.wireOp",EDGE,"E13.5.2");Q1=makeQuery(id+"F7.imprint","IMPRINT",FACE,{"disambiguationData":[TD([[makeQuery(id+"F7.imprint","IMPRINT",EDGE,{"derivedFrom":subQ1}),-1.0]])]});}
            var Q2;
            {var subQ1=sQuery(id+"F7.wireOp",EDGE,"E13.4.2");Q2=makeQuery(id+"F7.imprint","IMPRINT",FACE,{"disambiguationData":[TD([[makeQuery(id+"F7.imprint","IMPRINT",EDGE,{"derivedFrom":subQ1}),-1.0]])]});}
            var Q3;
            {var subQ1=sQuery(id+"F7.wireOp",EDGE,"E13.3.2");Q3=makeQuery(id+"F7.imprint","IMPRINT",FACE,{"disambiguationData":[TD([[makeQuery(id+"F7.imprint","IMPRINT",EDGE,{"derivedFrom":subQ1}),-1.0]])]});}
            var Q4;
            {var subQ1=sQuery(id+"F7.wireOp",EDGE,"E13.2.2");Q4=makeQuery(id+"F7.imprint","IMPRINT",FACE,{"disambiguationData":[TD([[makeQuery(id+"F7.imprint","IMPRINT",EDGE,{"derivedFrom":subQ1}),-1.0]])]});}
            var Q5;
            {var subQ1=sQuery(id+"F7.wireOp",EDGE,"E13.1.2");Q5=makeQuery(id+"F7.imprint","IMPRINT",FACE,{"disambiguationData":[TD([[makeQuery(id+"F7.imprint","IMPRINT",EDGE,{"derivedFrom":subQ1}),-1.0]])]});}
            var Q6;
            Q6=makeQuery(id+"F7.imprint","IMPRINT",FACE,{"disambiguationData":[TD([[makeQuery(id+"F7.imprint","IMPRINT",EDGE,{"derivedFrom":sQuery(id+"F7.wireOp",EDGE,"E9")}),1.0]])]});
            var Q7;
            {var subQ1=sQuery(id+"F7.wireOp",EDGE,"E13.47.2");Q7=makeQuery(id+"F7.imprint","IMPRINT",FACE,{"disambiguationData":[TD([[makeQuery(id+"F7.imprint","IMPRINT",EDGE,{"derivedFrom":subQ1}),-1.0]])]});}
            var Q8;
            {var subQ1=sQuery(id+"F7.wireOp",EDGE,"E13.46.2");Q8=makeQuery(id+"F7.imprint","IMPRINT",FACE,{"disambiguationData":[TD([[makeQuery(id+"F7.imprint","IMPRINT",EDGE,{"derivedFrom":subQ1}),-1.0]])]});}
            var Q9;
            {var subQ1=sQuery(id+"F7.wireOp",EDGE,"E13.45.2");Q9=makeQuery(id+"F7.imprint","IMPRINT",FACE,{"disambiguationData":[TD([[makeQuery(id+"F7.imprint","IMPRINT",EDGE,{"derivedFrom":subQ1}),-1.0]])]});}
            var Q10;
            {var subQ1=sQuery(id+"F7.wireOp",EDGE,"E13.44.2");Q10=makeQuery(id+"F7.imprint","IMPRINT",FACE,{"disambiguationData":[TD([[makeQuery(id+"F7.imprint","IMPRINT",EDGE,{"derivedFrom":subQ1}),-1.0]])]});}
            var Q11;
            {var subQ1=sQuery(id+"F7.wireOp",EDGE,"E13.43.2");Q11=makeQuery(id+"F7.imprint","IMPRINT",FACE,{"disambiguationData":[TD([[makeQuery(id+"F7.imprint","IMPRINT",EDGE,{"derivedFrom":subQ1}),-1.0]])]});}
            var Q12;
            {var subQ1=sQuery(id+"F7.wireOp",EDGE,"E13.42.2");Q12=makeQuery(id+"F7.imprint","IMPRINT",FACE,{"disambiguationData":[TD([[makeQuery(id+"F7.imprint","IMPRINT",EDGE,{"derivedFrom":subQ1}),-1.0]])]});}
            var Q13;
            {var subQ1=sQuery(id+"F7.wireOp",EDGE,"E13.41.2");Q13=makeQuery(id+"F7.imprint","IMPRINT",FACE,{"disambiguationData":[TD([[makeQuery(id+"F7.imprint","IMPRINT",EDGE,{"derivedFrom":subQ1}),-1.0]])]});}
            var Q14;
            {var subQ1=sQuery(id+"F7.wireOp",EDGE,"E13.40.2");Q14=makeQuery(id+"F7.imprint","IMPRINT",FACE,{"disambiguationData":[TD([[makeQuery(id+"F7.imprint","IMPRINT",EDGE,{"derivedFrom":subQ1}),-1.0]])]});}
            var Q15;
            {var subQ1=sQuery(id+"F7.wireOp",EDGE,"E13.39.2");Q15=makeQuery(id+"F7.imprint","IMPRINT",FACE,{"disambiguationData":[TD([[makeQuery(id+"F7.imprint","IMPRINT",EDGE,{"derivedFrom":subQ1}),-1.0]])]});}
            var Q16;
            {var subQ1=sQuery(id+"F7.wireOp",EDGE,"E13.38.2");Q16=makeQuery(id+"F7.imprint","IMPRINT",FACE,{"disambiguationData":[TD([[makeQuery(id+"F7.imprint","IMPRINT",EDGE,{"derivedFrom":subQ1}),-1.0]])]});}
            var Q17;
            {var subQ1=sQuery(id+"F7.wireOp",EDGE,"E13.37.2");Q17=makeQuery(id+"F7.imprint","IMPRINT",FACE,{"disambiguationData":[TD([[makeQuery(id+"F7.imprint","IMPRINT",EDGE,{"derivedFrom":subQ1}),-1.0]])]});}
            var Q18;
            {var subQ1=sQuery(id+"F7.wireOp",EDGE,"E13.36.2");Q18=makeQuery(id+"F7.imprint","IMPRINT",FACE,{"disambiguationData":[TD([[makeQuery(id+"F7.imprint","IMPRINT",EDGE,{"derivedFrom":subQ1}),-1.0]])]});}
            var Q19;
            {var subQ1=sQuery(id+"F7.wireOp",EDGE,"E13.35.2");Q19=makeQuery(id+"F7.imprint","IMPRINT",FACE,{"disambiguationData":[TD([[makeQuery(id+"F7.imprint","IMPRINT",EDGE,{"derivedFrom":subQ1}),-1.0]])]});}
            var Q20;
            {var subQ1=sQuery(id+"F7.wireOp",EDGE,"E13.34.2");Q20=makeQuery(id+"F7.imprint","IMPRINT",FACE,{"disambiguationData":[TD([[makeQuery(id+"F7.imprint","IMPRINT",EDGE,{"derivedFrom":subQ1}),-1.0]])]});}
            var Q21;
            {var subQ1=sQuery(id+"F7.wireOp",EDGE,"E13.33.2");Q21=makeQuery(id+"F7.imprint","IMPRINT",FACE,{"disambiguationData":[TD([[makeQuery(id+"F7.imprint","IMPRINT",EDGE,{"derivedFrom":subQ1}),-1.0]])]});}
            var Q22;
            {var subQ1=sQuery(id+"F7.wireOp",EDGE,"E13.32.2");Q22=makeQuery(id+"F7.imprint","IMPRINT",FACE,{"disambiguationData":[TD([[makeQuery(id+"F7.imprint","IMPRINT",EDGE,{"derivedFrom":subQ1}),-1.0]])]});}
            var Q23;
            {var subQ1=sQuery(id+"F7.wireOp",EDGE,"E13.31.2");Q23=makeQuery(id+"F7.imprint","IMPRINT",FACE,{"disambiguationData":[TD([[makeQuery(id+"F7.imprint","IMPRINT",EDGE,{"derivedFrom":subQ1}),-1.0]])]});}
            var Q24;
            {var subQ1=sQuery(id+"F7.wireOp",EDGE,"E13.30.2");Q24=makeQuery(id+"F7.imprint","IMPRINT",FACE,{"disambiguationData":[TD([[makeQuery(id+"F7.imprint","IMPRINT",EDGE,{"derivedFrom":subQ1}),-1.0]])]});}
            var Q25;
            {var subQ1=sQuery(id+"F7.wireOp",EDGE,"E13.29.2");Q25=makeQuery(id+"F7.imprint","IMPRINT",FACE,{"disambiguationData":[TD([[makeQuery(id+"F7.imprint","IMPRINT",EDGE,{"derivedFrom":subQ1}),-1.0]])]});}
            var Q26;
            {var subQ1=sQuery(id+"F7.wireOp",EDGE,"E13.28.2");Q26=makeQuery(id+"F7.imprint","IMPRINT",FACE,{"disambiguationData":[TD([[makeQuery(id+"F7.imprint","IMPRINT",EDGE,{"derivedFrom":subQ1}),-1.0]])]});}
            var Q27;
            {var subQ1=sQuery(id+"F7.wireOp",EDGE,"E13.27.2");Q27=makeQuery(id+"F7.imprint","IMPRINT",FACE,{"disambiguationData":[TD([[makeQuery(id+"F7.imprint","IMPRINT",EDGE,{"derivedFrom":subQ1}),-1.0]])]});}
            var Q28;
            {var subQ1=sQuery(id+"F7.wireOp",EDGE,"E13.26.2");Q28=makeQuery(id+"F7.imprint","IMPRINT",FACE,{"disambiguationData":[TD([[makeQuery(id+"F7.imprint","IMPRINT",EDGE,{"derivedFrom":subQ1}),-1.0]])]});}
            var Q29;
            {var subQ1=sQuery(id+"F7.wireOp",EDGE,"E13.25.2");Q29=makeQuery(id+"F7.imprint","IMPRINT",FACE,{"disambiguationData":[TD([[makeQuery(id+"F7.imprint","IMPRINT",EDGE,{"derivedFrom":subQ1}),-1.0]])]});}
            var Q30;
            {var subQ1=sQuery(id+"F7.wireOp",EDGE,"E13.24.2");Q30=makeQuery(id+"F7.imprint","IMPRINT",FACE,{"disambiguationData":[TD([[makeQuery(id+"F7.imprint","IMPRINT",EDGE,{"derivedFrom":subQ1}),-1.0]])]});}
            var Q31;
            {var subQ1=sQuery(id+"F7.wireOp",EDGE,"E13.23.2");Q31=makeQuery(id+"F7.imprint","IMPRINT",FACE,{"disambiguationData":[TD([[makeQuery(id+"F7.imprint","IMPRINT",EDGE,{"derivedFrom":subQ1}),-1.0]])]});}
            var Q32;
            {var subQ1=sQuery(id+"F7.wireOp",EDGE,"E13.22.2");Q32=makeQuery(id+"F7.imprint","IMPRINT",FACE,{"disambiguationData":[TD([[makeQuery(id+"F7.imprint","IMPRINT",EDGE,{"derivedFrom":subQ1}),-1.0]])]});}
            var Q33;
            {var subQ1=sQuery(id+"F7.wireOp",EDGE,"E13.21.2");Q33=makeQuery(id+"F7.imprint","IMPRINT",FACE,{"disambiguationData":[TD([[makeQuery(id+"F7.imprint","IMPRINT",EDGE,{"derivedFrom":subQ1}),-1.0]])]});}
            var Q34;
            {var subQ1=sQuery(id+"F7.wireOp",EDGE,"E13.20.2");Q34=makeQuery(id+"F7.imprint","IMPRINT",FACE,{"disambiguationData":[TD([[makeQuery(id+"F7.imprint","IMPRINT",EDGE,{"derivedFrom":subQ1}),-1.0]])]});}
            var Q35;
            {var subQ1=sQuery(id+"F7.wireOp",EDGE,"E13.19.2");Q35=makeQuery(id+"F7.imprint","IMPRINT",FACE,{"disambiguationData":[TD([[makeQuery(id+"F7.imprint","IMPRINT",EDGE,{"derivedFrom":subQ1}),-1.0]])]});}
            var Q36;
            {var subQ1=sQuery(id+"F7.wireOp",EDGE,"E13.18.2");Q36=makeQuery(id+"F7.imprint","IMPRINT",FACE,{"disambiguationData":[TD([[makeQuery(id+"F7.imprint","IMPRINT",EDGE,{"derivedFrom":subQ1}),-1.0]])]});}
            var Q37;
            {var subQ1=sQuery(id+"F7.wireOp",EDGE,"E13.17.2");Q37=makeQuery(id+"F7.imprint","IMPRINT",FACE,{"disambiguationData":[TD([[makeQuery(id+"F7.imprint","IMPRINT",EDGE,{"derivedFrom":subQ1}),-1.0]])]});}
            var Q38;
            {var subQ1=sQuery(id+"F7.wireOp",EDGE,"E13.16.2");Q38=makeQuery(id+"F7.imprint","IMPRINT",FACE,{"disambiguationData":[TD([[makeQuery(id+"F7.imprint","IMPRINT",EDGE,{"derivedFrom":subQ1}),-1.0]])]});}
            var Q39;
            {var subQ1=sQuery(id+"F7.wireOp",EDGE,"E13.15.2");Q39=makeQuery(id+"F7.imprint","IMPRINT",FACE,{"disambiguationData":[TD([[makeQuery(id+"F7.imprint","IMPRINT",EDGE,{"derivedFrom":subQ1}),-1.0]])]});}
            var Q40;
            {var subQ1=sQuery(id+"F7.wireOp",EDGE,"E13.14.2");Q40=makeQuery(id+"F7.imprint","IMPRINT",FACE,{"disambiguationData":[TD([[makeQuery(id+"F7.imprint","IMPRINT",EDGE,{"derivedFrom":subQ1}),-1.0]])]});}
            var Q41;
            {var subQ1=sQuery(id+"F7.wireOp",EDGE,"E13.13.2");Q41=makeQuery(id+"F7.imprint","IMPRINT",FACE,{"disambiguationData":[TD([[makeQuery(id+"F7.imprint","IMPRINT",EDGE,{"derivedFrom":subQ1}),-1.0]])]});}
            var Q42;
            {var subQ1=sQuery(id+"F7.wireOp",EDGE,"E13.12.2");Q42=makeQuery(id+"F7.imprint","IMPRINT",FACE,{"disambiguationData":[TD([[makeQuery(id+"F7.imprint","IMPRINT",EDGE,{"derivedFrom":subQ1}),-1.0]])]});}
            var Q43;
            {var subQ1=sQuery(id+"F7.wireOp",EDGE,"E13.11.2");Q43=makeQuery(id+"F7.imprint","IMPRINT",FACE,{"disambiguationData":[TD([[makeQuery(id+"F7.imprint","IMPRINT",EDGE,{"derivedFrom":subQ1}),-1.0]])]});}
            var Q44;
            {var subQ1=sQuery(id+"F7.wireOp",EDGE,"E13.10.2");Q44=makeQuery(id+"F7.imprint","IMPRINT",FACE,{"disambiguationData":[TD([[makeQuery(id+"F7.imprint","IMPRINT",EDGE,{"derivedFrom":subQ1}),-1.0]])]});}
            var Q45;
            {var subQ1=sQuery(id+"F7.wireOp",EDGE,"E13.9.2");Q45=makeQuery(id+"F7.imprint","IMPRINT",FACE,{"disambiguationData":[TD([[makeQuery(id+"F7.imprint","IMPRINT",EDGE,{"derivedFrom":subQ1}),-1.0]])]});}
            var Q46;
            {var subQ1=sQuery(id+"F7.wireOp",EDGE,"E13.8.2");Q46=makeQuery(id+"F7.imprint","IMPRINT",FACE,{"disambiguationData":[TD([[makeQuery(id+"F7.imprint","IMPRINT",EDGE,{"derivedFrom":subQ1}),-1.0]])]});}
            var Q47;
            {var subQ1=sQuery(id+"F7.wireOp",EDGE,"E13.7.2");Q47=makeQuery(id+"F7.imprint","IMPRINT",FACE,{"disambiguationData":[TD([[makeQuery(id+"F7.imprint","IMPRINT",EDGE,{"derivedFrom":subQ1}),-1.0]])]});}
            extrude(context, id + "F8", {"entities" : qUnion([Q0, Q1, Q2, Q3, Q4, Q5, Q6, Q7, Q8, Q9, Q10, Q11, Q12, Q13, Q14, Q15, Q16, Q17, Q18, Q19, Q20, Q21, Q22, Q23, Q24, Q25, Q26, Q27, Q28, Q29, Q30, Q31, Q32, Q33, Q34, Q35, Q36, Q37, Q38, Q39, Q40, Q41, Q42, Q43, Q44, Q45, Q46, Q47]), "operationType" : NewBodyOperationType.REMOVE, "oppositeDirection" : true, "depth" : 25 * mm, "offsetDistance" : 25 * mm});
        }
        {
            var Q0;
            Q0=qCreatedBy(makeId("Front.planeOp"),FACE);
            var sketch = newSketch(context, id + "F9", { "sketchPlane" : qUnion([Q0])});
            skLineSegment(sketch, "E14", {"start": v(-30.46, 0) * mm, "end": v(10.56, 0) * mm, "construction": true});
            skLineSegment(sketch, "E15", {"start": v(-5, 24.43) * mm, "end": v(-5, -19.5) * mm, "construction": true});
            skPoint(sketch, "E16", {"position": v(-5, 0) * mm});
            skCircle(sketch, "E17", {"center": v(-5, 0) * mm, "radius": 3 * mm});
            skSolve(sketch);
        }
        {
            var Q0;
            Q0 = qSketchRegion(id + "F9", true);
            extrude(context, id + "F10", {"entities" : qUnion([Q0]), "operationType" : NewBodyOperationType.REMOVE, "oppositeDirection" : true, "depth" : 25 * mm, "offsetDistance" : 25 * mm});
        }
        {
            var Q0;
            Q0=makeQuery(id+"F10.boolean.opBoolean","INTERSECT",EDGE,{"derivedFrom":[makeQuery(id+"F6.boolean.opBoolean","COPY",FACE,{"derivedFrom":makeQuery(id+"F6.opExtrude","SWEPT_FACE",FACE,{"disambiguationData":[OSD([sQuery(id+"F5.wireOp",EDGE,"E2")])]})}),makeQuery(id+"F10.opExtrude","SWEPT_FACE",FACE,{"disambiguationData":[OSD([sQuery(id+"F9.wireOp",EDGE,"E17")])]})]});
            chamfer(context, id + "F11", {"entities" : qUnion([Q0]), "width" : 0.5 * mm, "tangentPropagation" : true});
        }
    });
